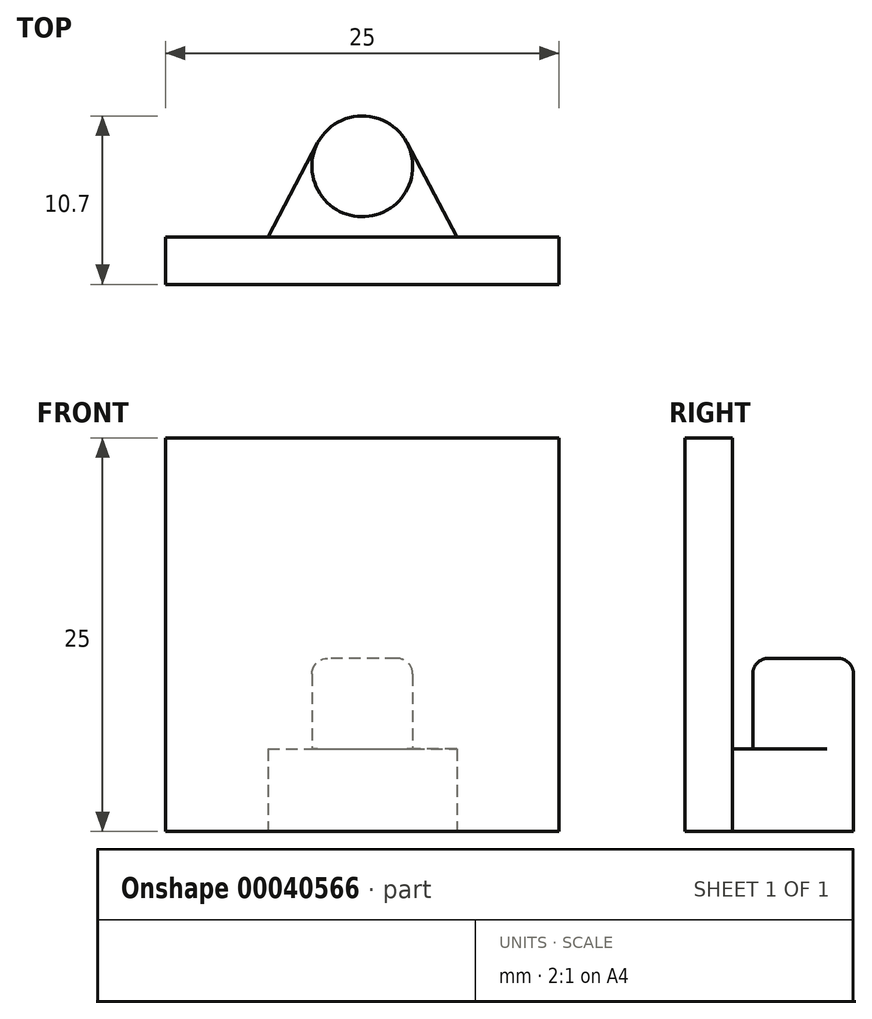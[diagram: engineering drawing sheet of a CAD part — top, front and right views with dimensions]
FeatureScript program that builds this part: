
annotation { "Feature Type Name" : "Feature", "Feature Type Description" : "" }
export const myFeature = defineFeature(function(context is Context, id is Id, definition is map)
    precondition{}
    {
        {
            var Q0;
            Q0=qCreatedBy(makeId("Top.planeOp"),FACE);
            var sketch = newSketch(context, id + "F0", { "sketchPlane" : qUnion([Q0])});
            skLineSegment(sketch, "E0.bottom", {"start": v(0, 0) * mm, "end": v(25, 0) * mm});
            skLineSegment(sketch, "E0.top", {"start": v(0, 3) * mm, "end": v(25, 3) * mm});
            skLineSegment(sketch, "E0.left", {"start": v(0, 0) * mm, "end": v(0, 3) * mm});
            skLineSegment(sketch, "E0.right", {"start": v(25, 0) * mm, "end": v(25, 3) * mm});
            skLineSegment(sketch, "E1", {"start": v(12.5, 3) * mm, "end": v(12.5, 7.5) * mm});
            skCircle(sketch, "E2", {"center": v(12.5, 7.5) * mm, "radius": 3.2 * mm});
            skLineSegment(sketch, "E3", {"start": v(6.5, 3) * mm, "end": v(9.67, 9) * mm});
            skLineSegment(sketch, "E4.MirrorCS", {"start": v(18.5, 3) * mm, "end": v(15.33, 9) * mm});
            skSolve(sketch);
        }
        {
            var Q0;
            Q0=makeQuery(id+"F0.imprint","IMPRINT",FACE,{"disambiguationData":[TD([[makeQuery(id+"F0.imprint","IMPRINT",EDGE,{"derivedFrom":sQuery(id+"F0.wireOp",EDGE,"E0.bottom")}),1.0]])]});
            extrude(context, id + "F1", {"entities" : qUnion([Q0]), "depth" : 25 * mm});
        }
        {
            var Q0;
            {var subQ0=sQuery(id+"F0.wireOp",EDGE,"E3");Q0=makeQuery(id+"F0.imprint","IMPRINT",FACE,{"disambiguationData":[TD([[makeQuery(id+"F0.imprint","IMPRINT",EDGE,{"derivedFrom":subQ0}),-1.0]])]});}
            var Q1;
            {var subQ0=sQuery(id+"F0.wireOp",EDGE,"E4.MirrorCS");Q1=makeQuery(id+"F0.imprint","IMPRINT",FACE,{"disambiguationData":[TD([[makeQuery(id+"F0.imprint","IMPRINT",EDGE,{"derivedFrom":subQ0}),1.0]])]});}
            extrude(context, id + "F2", {"entities" : qUnion([Q0, Q1]), "operationType" : NewBodyOperationType.ADD, "depth" : 5.25 * mm});
        }
        {
            var Q0;
            {var subQ0=sQuery(id+"F0.wireOp",EDGE,"E2");var subQ3=makeQuery(id+"F0.imprint","INTERSECT",VERTEX,{"derivedFrom":[subQ0,sQuery(id+"F0.wireOp",EDGE,"E3")]});Q0=makeQuery(id+"F0.imprint","IMPRINT",FACE,{"disambiguationData":[TD([[makeQuery(id+"F0.imprint","IMPRINT",EDGE,{"disambiguationData":[TD([[subQ3,1.0]])],"derivedFrom":subQ0}),1.0]])]});}
            extrude(context, id + "F3", {"entities" : qUnion([Q0]), "operationType" : NewBodyOperationType.ADD, "depth" : 11 * mm});
        }
        {
            var Q0;
            Q0=makeQuery(id+"F2.opExtrude","SWEPT_EDGE",EDGE,{"disambiguationData":[OSD([sQuery(id+"F0.wireOp",EDGE,"E0.top"),sQuery(id+"F0.wireOp",EDGE,"E4.MirrorCS")])]});
            var Q1;
            Q1=makeQuery(id+"F2.opExtrude","CAP_EDGE",EDGE,{"disambiguationData":[OSD([sQuery(id+"F0.wireOp",EDGE,"E0.top")])],"isStart":false});
            var Q2;
            Q2=makeQuery(id+"F2.opExtrude","SWEPT_EDGE",EDGE,{"disambiguationData":[OSD([sQuery(id+"F0.wireOp",EDGE,"E0.top"),sQuery(id+"F0.wireOp",EDGE,"E3")])]});
            var Q3;
            Q3=makeQuery(id+"F3.opExtrude","CAP_EDGE",EDGE,{"disambiguationData":[OSD([sQuery(id+"F0.wireOp",EDGE,"E2")])],"isStart":false});
            var Q4;
            Q4=makeQuery(id+"F2.opExtrude","CAP_EDGE",EDGE,{"disambiguationData":[OSD([sQuery(id+"F0.wireOp",EDGE,"E2")])],"isStart":false});
            fillet(context, id + "F4", {"entities" : qUnion([Q0, Q1, Q2, Q3, Q4]), "radius" : 1 * mm, "tangentPropagation" : true, "allowEdgeOverflow" : false});
        }
    });
